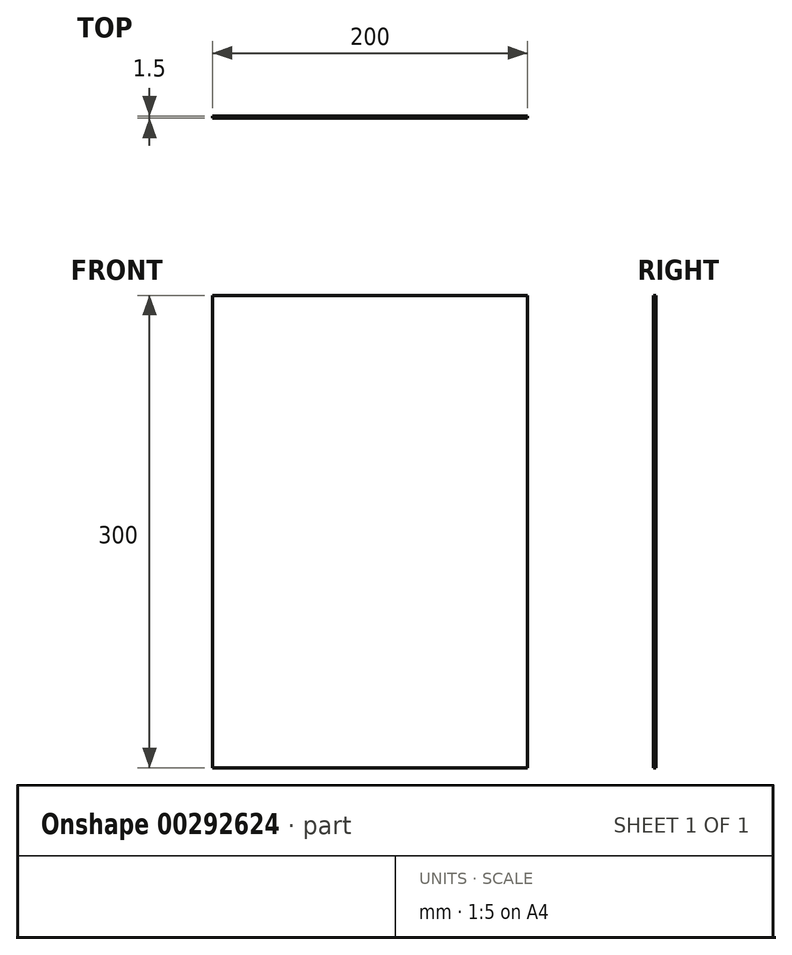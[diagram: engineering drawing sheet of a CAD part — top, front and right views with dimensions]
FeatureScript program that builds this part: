
annotation { "Feature Type Name" : "Feature", "Feature Type Description" : "" }
export const myFeature = defineFeature(function(context is Context, id is Id, definition is map)
    precondition{}
    {
        {
            var Q0;
            Q0=qCreatedBy(makeId("Front.planeOp"),FACE);
            var sketch = newSketch(context, id + "F0", { "sketchPlane" : qUnion([Q0])});
            skLineSegment(sketch, "E0.bottom", {"start": v(0, 0) * mm, "end": v(200, 0) * mm});
            skLineSegment(sketch, "E0.top", {"start": v(0, 300) * mm, "end": v(200, 300) * mm});
            skLineSegment(sketch, "E0.left", {"start": v(0, 0) * mm, "end": v(0, 300) * mm});
            skLineSegment(sketch, "E0.right", {"start": v(200, 0) * mm, "end": v(200, 300) * mm});
            skSolve(sketch);
        }
        {
            var Q0;
            Q0=makeQuery(id+"F0.imprint","IMPRINT",FACE,{"disambiguationData":[TD([[makeQuery(id+"F0.imprint","IMPRINT",EDGE,{"derivedFrom":sQuery(id+"F0.wireOp",EDGE,"E0.bottom")}),1.0]])]});
            extrude(context, id + "F1", {"entities" : qUnion([Q0]), "depth" : 1.5 * mm});
        }
    });
